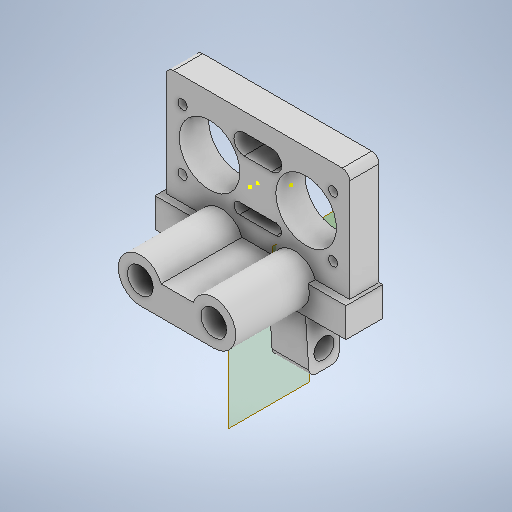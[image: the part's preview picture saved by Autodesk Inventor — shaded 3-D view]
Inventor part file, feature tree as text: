
AUTODESK INVENTOR PART (.ipt)
format: ipt  version: 2025.2 (Build 292293000, 293)  size: 439,808 bytes
history: native  units: mm
features: sketch x13, extrude x9, other x4, mirror x3, fillet x2, hole x1
ambient origin geometry x8: Origin, YZ Plane, XZ Plane, XY Plane, X Axis, Y Axis, Z Axis, Center Point
bodies: Body1 (feature_tree)
feature tree (32):
  other  "Bryła1"
  extrude  "Wyciągnięcie proste1"  Depth=50.0mm
  hole  "Otwór2"  [1 undecoded]
  extrude  "Wyciągnięcie proste3"  Depth=8.0mm TaperAngle=0.0deg
  mirror  "Odbij1"
  extrude  "Wyciągnięcie proste4"  Depth=41.0mm
  fillet  "Zaokrąglenie1"  Radius=16.5mm
  extrude  "Wyciągnięcie proste5"  Depth=45.0mm
  other  "Płaszczyzna konstrukcyjna3"
  other  "Płaszczyzna konstrukcyjna2"
  other  "Płaszczyzna konstrukcyjna1"
  extrude  "Wyciągnięcie proste13"  Depth=20.0mm
  sketch  "Szkic23"
  sketch  "Szkic24"
  extrude  "Wyciągnięcie proste14"  Depth=16.5mm
  mirror  "Odbij4"
  sketch  "Szkic26"
  extrude  "Wyciągnięcie proste15"  Depth=9.35mm
  extrude  "Wyciągnięcie proste16"  Depth=10.0mm
  fillet  "Zaokrąglenie4"  Radius=8.0mm
  mirror  "Odbij5"
  extrude  "Wyciągnięcie proste17"  Depth=45.0mm
  sketch  "Szkic1"
  sketch  "Szkic8"
  sketch  "Szkic9"
  sketch  "Szkic10"
  sketch  "Szkic11"
  sketch  "Szkic22"
  sketch  "Szkic25"
  sketch  "Szkic27"
  sketch  "Szkic28"
  sketch  "Szkic29"
note: 1 required parameter value undecoded (feature->parameter linkage not recoverable at this tier; creation-order binding heuristic only, values carry confidence <= 0.55)
